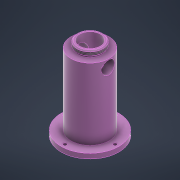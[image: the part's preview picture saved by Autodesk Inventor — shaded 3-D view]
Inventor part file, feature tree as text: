
AUTODESK INVENTOR PART (.ipt)
format: ipt  version: 2022 (Build 260153000, 153)  size: 250,368 bytes
history: native  units: mm
features: sketch x4, hole x3, thread x2, revolve x1, plane x1, pattern_circular x1, extrude x1, projected_geometry x1
ambient origin geometry x8: Origin, YZ Plane, XZ Plane, XY Plane, X Axis, Y Axis, Z Axis, Center Point
bodies: Solid1 (feature_tree)
feature tree (14):
  revolve  "Revolution1"  [1 undecoded]
  plane  "Work Plane1"
  hole  "Hole1"  [1 undecoded]
  thread  "Thread1"  [1 undecoded]
  thread  "Thread2"  [1 undecoded]
  hole  "Hole2"  [1 undecoded]
  pattern_circular  "Circular Pattern1"  Angle=90.0deg  [1 undecoded]
  extrude  "Extrusion1"  TaperAngle=135.0deg  [1 undecoded]
  hole  "Hole3"  [1 undecoded]
  sketch  "Sketch2"  dims[d0=26.0mm d1=35.0mm]
  sketch  "Sketch3"  dims[d8=56.0mm d11=24.0mm d13=135.0deg d14=135.0deg d15=22.0mm]
  sketch  "Sketch4"  dims[d16=22.0mm d18=3.0mm]
  sketch  "Sketch5"  dims[d22=19.0mm d25=90.0deg d26=135.0deg d28=6.0mm d30=18.0mm d38=8.0mm d39=2.0mm d40=18.5mm d41=7.0mm d42=12.0mm d43=6.0mm d44=10.4mm d45=2.0mm d46=90.0deg d47=8.0mm d48=20.594885mm d50=14.0mm d55=3.5mm d56=0.0mm d57=2.0mm d58=0.0mm d59=20.0mm d60=2.0mm d61=3.5mm d62=0.6mm d63=3.0mm d64=2.0mm d65=10.0mm d66=8.0mm d67=135.0deg d68=53.0mm d69=11.0mm d70=4.5mm d71=23.0mm d72=3.1mm d73=6.0mm d74=6.3mm d75=4.775mm d76=90.0deg d77=8.8mm d78=20.594885mm d79=40.0mm d80=360.0deg d82=3.5mm d83=0.0mm d84=2.013mm d85=5.0mm d86=4.4mm d87=2.0mm d88=90.0deg d89=5.0mm d90=20.594885mm]
  projected_geometry  "Projected Loop1"
note: 8 required parameter values undecoded (feature->parameter linkage not recoverable at this tier; creation-order binding heuristic only, values carry confidence <= 0.55)